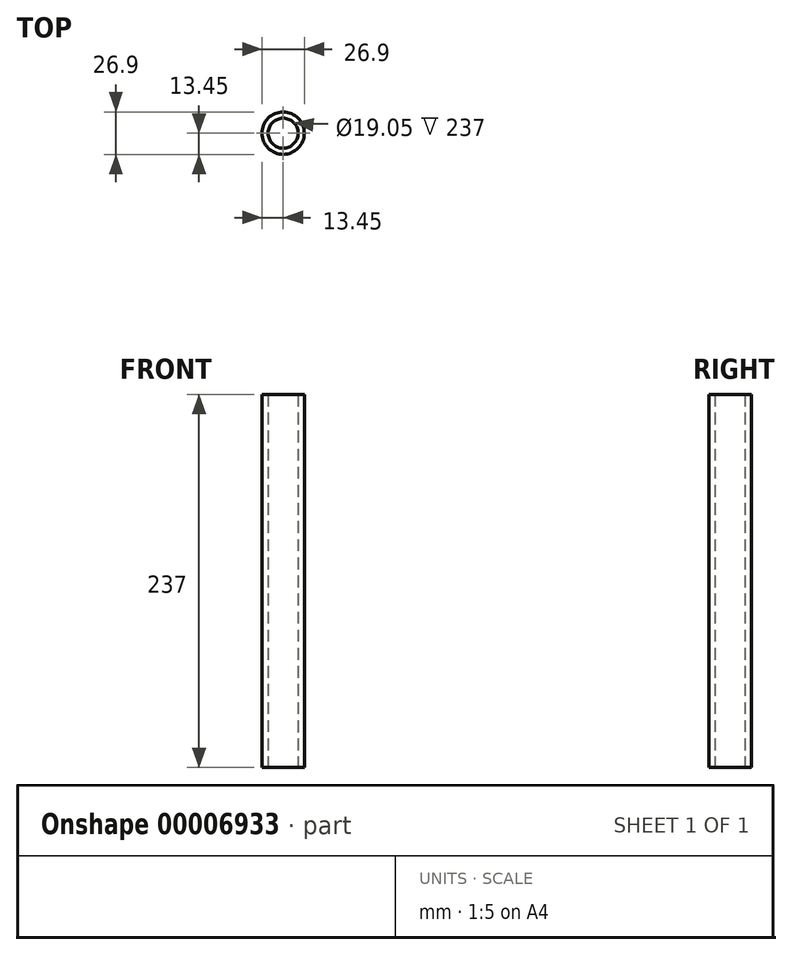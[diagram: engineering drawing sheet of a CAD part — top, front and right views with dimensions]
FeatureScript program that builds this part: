
annotation { "Feature Type Name" : "Feature", "Feature Type Description" : "" }
export const myFeature = defineFeature(function(context is Context, id is Id, definition is map)
    precondition{}
    {
        {
            var Q0;
            Q0=qCreatedBy(makeId("Top.planeOp"),FACE);
            var sketch = newSketch(context, id + "F0", { "sketchPlane" : qUnion([Q0])});
            skCircle(sketch, "E0", {"center": v(0, 0) * mm, "radius": 13.45 * mm});
            skCircle(sketch, "E1", {"center": v(0, 0) * mm, "radius": 9.53 * mm});
            skSolve(sketch);
        }
        {
            var Q0;
            Q0=makeQuery(id+"F0.imprint","IMPRINT",FACE,{"disambiguationData":[TD([[makeQuery(id+"F0.imprint","IMPRINT",EDGE,{"derivedFrom":sQuery(id+"F0.wireOp",EDGE,"E0")}),1.0]])]});
            extrude(context, id + "F1", {"entities" : qUnion([Q0]), "depth" : 237 * mm});
        }
    });
